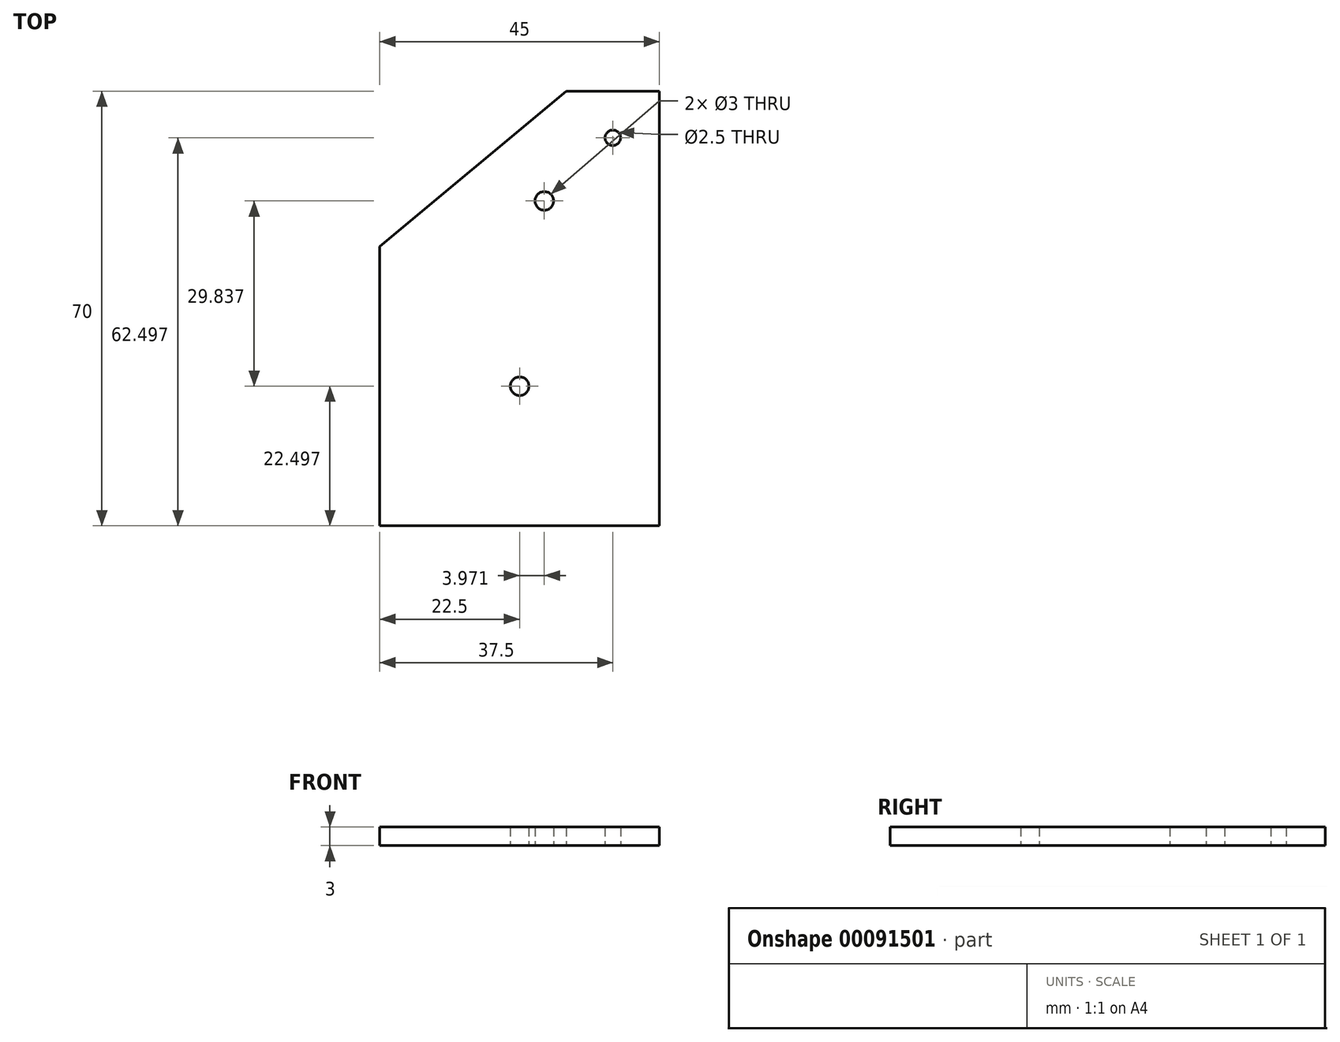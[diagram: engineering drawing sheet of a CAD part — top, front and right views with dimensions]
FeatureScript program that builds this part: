
annotation { "Feature Type Name" : "Feature", "Feature Type Description" : "" }
export const myFeature = defineFeature(function(context is Context, id is Id, definition is map)
    precondition{}
    {
        {
            var Q0;
            Q0=qCreatedBy(makeId("Top.planeOp"),FACE);
            var sketch = newSketch(context, id + "F0", { "sketchPlane" : qUnion([Q0])});
            skLineSegment(sketch, "E0", {"start": v(0, -41.62) * mm, "end": v(0, 28.38) * mm});
            skLineSegment(sketch, "E1", {"start": v(0, -41.62) * mm, "end": v(-45, -41.62) * mm});
            skLineSegment(sketch, "E2", {"start": v(0, 28.38) * mm, "end": v(-15, 28.38) * mm});
            skLineSegment(sketch, "E3", {"start": v(-45, -41.62) * mm, "end": v(-45, 3.38) * mm});
            skLineSegment(sketch, "E4", {"start": v(-45, 3.38) * mm, "end": v(-15, 28.38) * mm});
            skLineSegment(sketch, "E5", {"start": v(-45, 3.38) * mm, "end": v(0, -41.62) * mm, "construction": true});
            skLineSegment(sketch, "E6", {"start": v(-45, 3.38) * mm, "end": v(0, 3.38) * mm, "construction": true});
            skLineSegment(sketch, "E7", {"start": v(-45, -41.62) * mm, "end": v(0, 3.38) * mm, "construction": true});
            skPoint(sketch, "E8", {"position": v(-22.5, -19.12) * mm});
            skLineSegment(sketch, "E9", {"start": v(-15, 28.38) * mm, "end": v(-15, 13.38) * mm, "construction": true});
            skLineSegment(sketch, "E10", {"start": v(-15, 13.38) * mm, "end": v(0, 13.38) * mm, "construction": true});
            skLineSegment(sketch, "E11", {"start": v(-15, 28.38) * mm, "end": v(0, 13.38) * mm, "construction": true});
            skLineSegment(sketch, "E12", {"start": v(-15, 13.38) * mm, "end": v(0, 28.38) * mm, "construction": true});
            skPoint(sketch, "E13", {"position": v(-7.5, 20.88) * mm});
            skCircle(sketch, "E14", {"center": v(-7.5, 20.88) * mm, "radius": 5 * mm, "construction": true});
            skCircle(sketch, "E15", {"center": v(-22.5, -19.12) * mm, "radius": 20 * mm, "construction": true});
            skLineSegment(sketch, "E16", {"start": v(-63.54, 25.37) * mm, "end": v(-63.54, 5.37) * mm, "construction": true});
            skLineSegment(sketch, "E17", {"start": v(-7.5, 13.38) * mm, "end": v(-7.5, 15.88) * mm, "construction": true});
            skLineSegment(sketch, "E18", {"start": v(28.13, -4.98) * mm, "end": v(28.13, -9.98) * mm, "construction": true});
            skCircle(sketch, "E19", {"center": v(-18.53, 10.71) * mm, "radius": 10 * mm, "construction": true});
            skSolve(sketch);
        }
        {
            var Q0;
            Q0=makeQuery(id+"F0.imprint","IMPRINT",FACE,{"disambiguationData":[TD([[makeQuery(id+"F0.imprint","IMPRINT",EDGE,{"derivedFrom":sQuery(id+"F0.wireOp",EDGE,"E0")}),1.0]])]});
            var Q1;
            Q1=sQuery(id+"F0.wireOp",EDGE,"E0");
            extrude(context, id + "F1", {"entities" : qUnion([Q0]), "surfaceEntities" : qUnion([Q1]), "depth" : 3 * mm});
        }
        {
            var Q0;
            Q0=sQuery(id+"F0.wireOp",VERTEX,"E8");
            var Q1;
            Q1=makeQuery(id+"F1.opExtrude","SWEPT_BODY",BODY,{"disambiguationData":[OSD([sQuery(id+"F0.wireOp",EDGE,"E0"),sQuery(id+"F0.wireOp",EDGE,"E1"),sQuery(id+"F0.wireOp",EDGE,"E2"),sQuery(id+"F0.wireOp",EDGE,"E3"),sQuery(id+"F0.wireOp",EDGE,"E4")])]});
            hole(context, id + "F2", {"style" : HoleStyle.SIMPLE, "endStyle" : HoleEndStyle.THROUGH, "oppositeDirection" : true, "holeDiameter" : 3 * mm, "locations" : qUnion([Q0]), "scope" : qUnion([Q1]), "isTappedThrough" : true});
        }
        {
            var Q0;
            Q0=sQuery(id+"F0.wireOp",VERTEX,"E19.center");
            var Q1;
            Q1=makeQuery(id+"F1.opExtrude","SWEPT_BODY",BODY,{"disambiguationData":[OSD([sQuery(id+"F0.wireOp",EDGE,"E0"),sQuery(id+"F0.wireOp",EDGE,"E1"),sQuery(id+"F0.wireOp",EDGE,"E2"),sQuery(id+"F0.wireOp",EDGE,"E3"),sQuery(id+"F0.wireOp",EDGE,"E4")])]});
            hole(context, id + "F3", {"style" : HoleStyle.SIMPLE, "endStyle" : HoleEndStyle.THROUGH, "oppositeDirection" : true, "holeDiameter" : 3 * mm, "locations" : qUnion([Q0]), "scope" : qUnion([Q1]), "isTappedThrough" : true});
        }
        {
            var Q0;
            Q0=sQuery(id+"F0.wireOp",VERTEX,"E13");
            var Q1;
            Q1=makeQuery(id+"F1.opExtrude","SWEPT_BODY",BODY,{"disambiguationData":[OSD([sQuery(id+"F0.wireOp",EDGE,"E0"),sQuery(id+"F0.wireOp",EDGE,"E1"),sQuery(id+"F0.wireOp",EDGE,"E2"),sQuery(id+"F0.wireOp",EDGE,"E3"),sQuery(id+"F0.wireOp",EDGE,"E4")])]});
            hole(context, id + "F4", {"style" : HoleStyle.SIMPLE, "endStyle" : HoleEndStyle.THROUGH, "oppositeDirection" : true, "holeDiameter" : 2.5 * mm, "locations" : qUnion([Q0]), "scope" : qUnion([Q1]), "isTappedThrough" : true});
        }
    });
